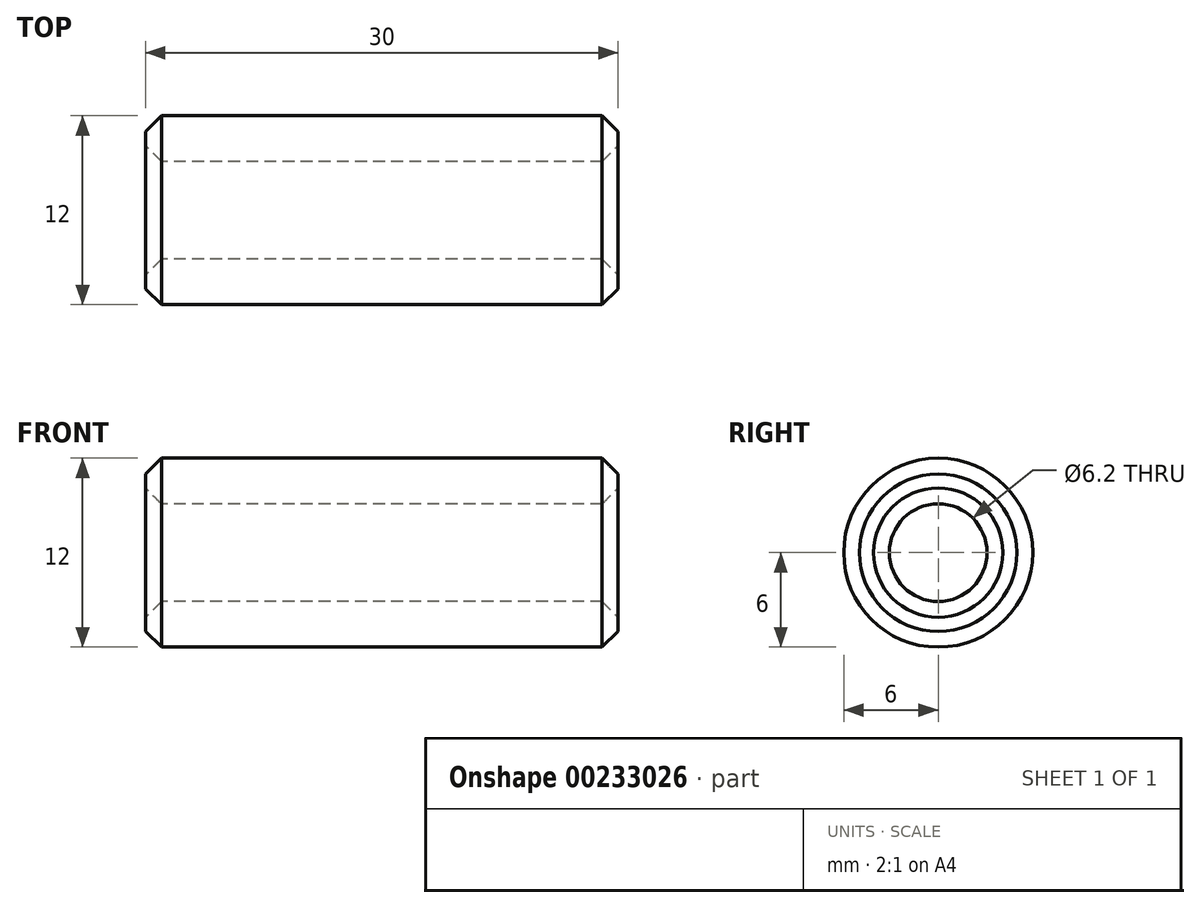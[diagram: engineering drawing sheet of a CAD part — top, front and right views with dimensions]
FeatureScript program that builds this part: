
annotation { "Feature Type Name" : "Feature", "Feature Type Description" : "" }
export const myFeature = defineFeature(function(context is Context, id is Id, definition is map)
    precondition{}
    {
        {
            var Q0;
            Q0=qCreatedBy(makeId("Front.planeOp"),FACE);
            var sketch = newSketch(context, id + "F0", { "sketchPlane" : qUnion([Q0])});
            skLineSegment(sketch, "E0.bottom", {"start": v(0, 3.1) * mm, "end": v(30, 3.1) * mm});
            skLineSegment(sketch, "E0.top", {"start": v(0, 6) * mm, "end": v(30, 6) * mm});
            skLineSegment(sketch, "E0.left", {"start": v(0, 3.1) * mm, "end": v(0, 6) * mm});
            skLineSegment(sketch, "E0.right", {"start": v(30, 3.1) * mm, "end": v(30, 6) * mm});
            skLineSegment(sketch, "E1", {"start": v(-7.44, 0) * mm, "end": v(41.07, 0) * mm, "construction": true});
            skSolve(sketch);
        }
        {
            var Q0;
            Q0=makeQuery(id+"F0.imprint","IMPRINT",FACE,{"disambiguationData":[TD([[makeQuery(id+"F0.imprint","IMPRINT",EDGE,{"derivedFrom":sQuery(id+"F0.wireOp",EDGE,"E0.bottom")}),1.0]])]});
            var Q1;
            Q1=sQuery(id+"F0.wireOp",EDGE,"E1");
            revolve(context, id + "F1", {"entities" : qUnion([Q0]), "axis" : qUnion([Q1]), "revolveType" : RevolveType.FULL});
        }
        {
            var Q0;
            Q0=makeQuery(id+"F1.opRevolve","SWEPT_FACE",FACE,{"disambiguationData":[OSD([sQuery(id+"F0.wireOp",EDGE,"E0.right")])]});
            var Q1;
            Q1=makeQuery(id+"F1.opRevolve","SWEPT_FACE",FACE,{"disambiguationData":[OSD([sQuery(id+"F0.wireOp",EDGE,"E0.left")])]});
            chamfer(context, id + "F2", {"entities" : qUnion([Q0, Q1]), "width" : 1 * mm, "tangentPropagation" : true});
        }
    });
